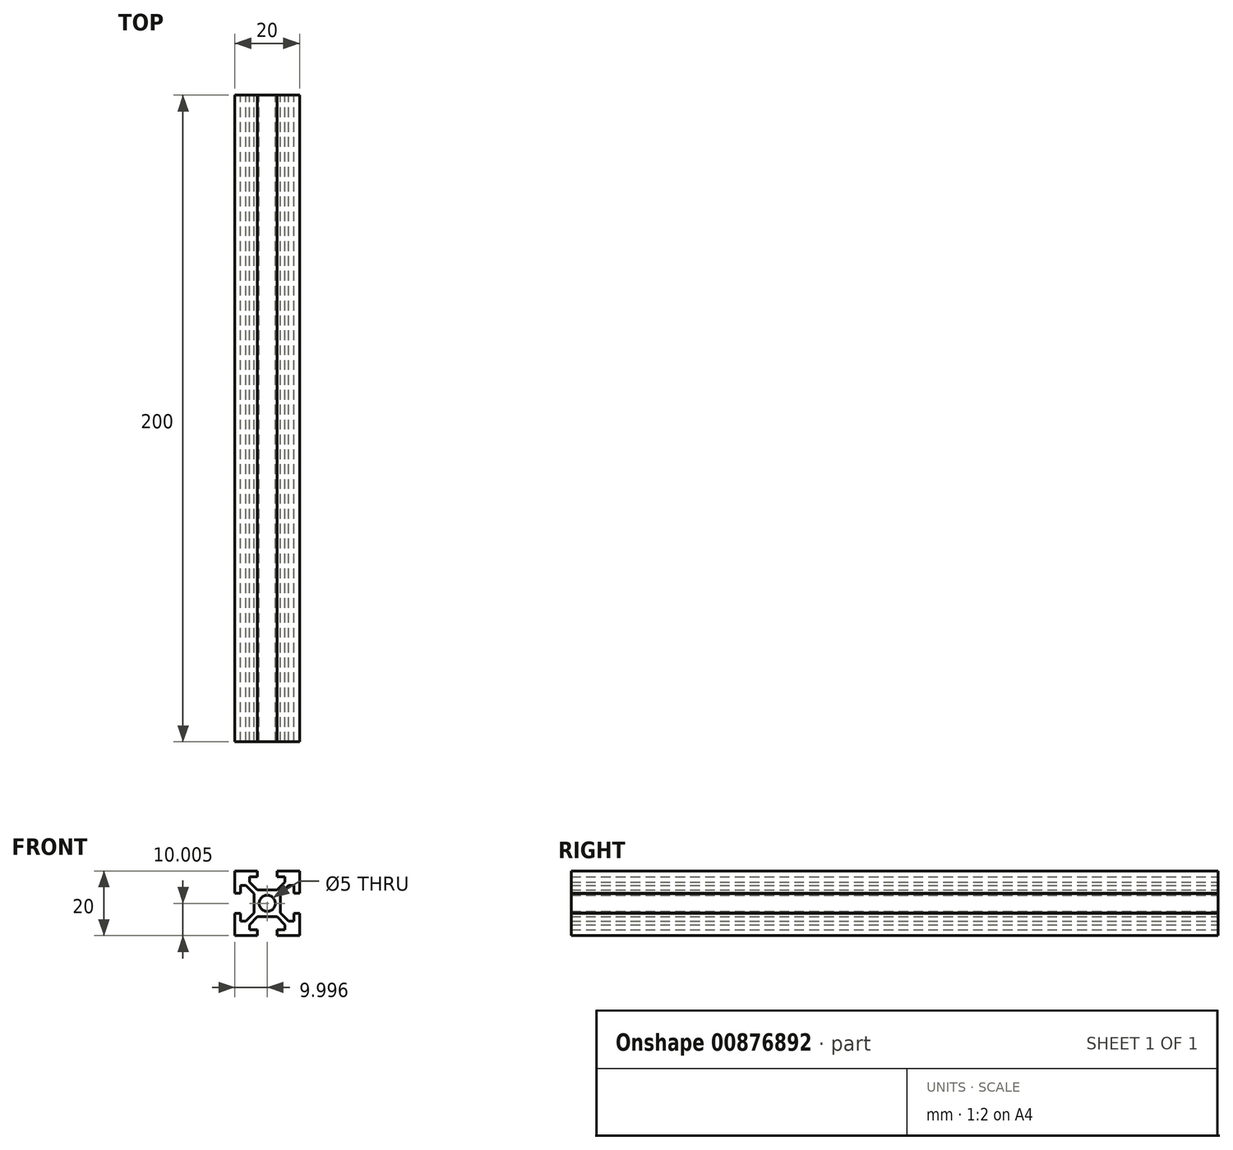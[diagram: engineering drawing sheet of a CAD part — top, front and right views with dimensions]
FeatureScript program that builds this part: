
annotation { "Feature Type Name" : "Feature", "Feature Type Description" : "" }
export const myFeature = defineFeature(function(context is Context, id is Id, definition is map)
    precondition{}
    {
        {
            var Q0;
            Q0=qCreatedBy(makeId("Front.planeOp"),FACE);
            var sketch = newSketch(context, id + "F0", { "sketchPlane" : qUnion([Q0])});
            skLineSegment(sketch, "E0.bottom", {"start": v(-42.2, 33.21) * mm, "end": v(-22.2, 33.21) * mm});
            skLineSegment(sketch, "E0.top", {"start": v(-42.2, 13.21) * mm, "end": v(-22.2, 13.21) * mm});
            skLineSegment(sketch, "E0.left", {"start": v(-42.2, 33.21) * mm, "end": v(-42.2, 13.21) * mm});
            skLineSegment(sketch, "E0.right", {"start": v(-22.2, 33.21) * mm, "end": v(-22.2, 13.21) * mm});
            skPoint(sketch, "E0.middle", {"position": v(-32.2, 23.21) * mm});
            skLineSegment(sketch, "E1", {"start": v(-24, 26.31) * mm, "end": v(-22.2, 26.31) * mm});
            skLineSegment(sketch, "E2.MirrorCS", {"start": v(-24, 20.11) * mm, "end": v(-22.2, 20.11) * mm});
            skLineSegment(sketch, "E3", {"start": v(-24, 26.31) * mm, "end": v(-24, 28.71) * mm});
            skLineSegment(sketch, "E4.MirrorCS", {"start": v(-24, 20.11) * mm, "end": v(-24, 17.71) * mm});
            skLineSegment(sketch, "E5", {"start": v(-24, 28.71) * mm, "end": v(-25.6, 28.71) * mm});
            skLineSegment(sketch, "E6.MirrorCS", {"start": v(-24, 17.71) * mm, "end": v(-25.6, 17.71) * mm});
            skCircle(sketch, "E7", {"center": v(-32.2, 23.21) * mm, "radius": 2.5 * mm});
            skLineSegment(sketch, "E8", {"start": v(-28.1, 26.21) * mm, "end": v(-28.1, 20.21) * mm});
            skLineSegment(sketch, "E9", {"start": v(-28.1, 26.21) * mm, "end": v(-25.6, 28.71) * mm});
            skLineSegment(sketch, "E10.MirrorCS", {"start": v(-28.1, 20.21) * mm, "end": v(-25.6, 17.71) * mm});
            skLineSegment(sketch, "E11.MirrorCS", {"start": v(-40.4, 26.31) * mm, "end": v(-42.2, 26.31) * mm});
            skLineSegment(sketch, "E12.MirrorCS", {"start": v(-40.4, 26.31) * mm, "end": v(-40.4, 28.71) * mm});
            skLineSegment(sketch, "E13.MirrorCS", {"start": v(-40.4, 28.71) * mm, "end": v(-38.8, 28.71) * mm});
            skLineSegment(sketch, "E14.MirrorCS", {"start": v(-36.3, 26.21) * mm, "end": v(-38.8, 28.71) * mm});
            skLineSegment(sketch, "E15.MirrorCS", {"start": v(-36.3, 26.21) * mm, "end": v(-36.3, 20.21) * mm});
            skLineSegment(sketch, "E16.MirrorCS", {"start": v(-36.3, 20.21) * mm, "end": v(-38.8, 17.71) * mm});
            skLineSegment(sketch, "E17.MirrorCS", {"start": v(-40.4, 17.71) * mm, "end": v(-38.8, 17.71) * mm});
            skLineSegment(sketch, "E18.MirrorCS", {"start": v(-40.4, 20.11) * mm, "end": v(-40.4, 17.71) * mm});
            skLineSegment(sketch, "E19.MirrorCS", {"start": v(-40.4, 20.11) * mm, "end": v(-42.2, 20.11) * mm});
            skLineSegment(sketch, "E20", {"start": v(-35.3, 33.21) * mm, "end": v(-35.3, 31.41) * mm});
            skLineSegment(sketch, "E21", {"start": v(-35.3, 31.41) * mm, "end": v(-37.7, 31.41) * mm});
            skLineSegment(sketch, "E22", {"start": v(-37.7, 31.41) * mm, "end": v(-37.7, 29.81) * mm});
            skLineSegment(sketch, "E23", {"start": v(-35.2, 27.31) * mm, "end": v(-32.2, 27.31) * mm});
            skLineSegment(sketch, "E24.MirrorCS", {"start": v(-29.1, 33.21) * mm, "end": v(-29.1, 31.41) * mm});
            skLineSegment(sketch, "E25.MirrorCS", {"start": v(-29.1, 31.41) * mm, "end": v(-26.7, 31.41) * mm});
            skLineSegment(sketch, "E26.MirrorCS", {"start": v(-26.7, 31.41) * mm, "end": v(-26.7, 29.81) * mm});
            skLineSegment(sketch, "E27.MirrorCS", {"start": v(-29.2, 27.31) * mm, "end": v(-32.2, 27.31) * mm});
            skLineSegment(sketch, "E28", {"start": v(-26.7, 29.81) * mm, "end": v(-29.2, 27.31) * mm});
            skLineSegment(sketch, "E29", {"start": v(-37.7, 29.81) * mm, "end": v(-35.2, 27.31) * mm});
            skLineSegment(sketch, "E30.MirrorCS", {"start": v(-35.3, 13.21) * mm, "end": v(-35.3, 15.01) * mm});
            skLineSegment(sketch, "E31.MirrorCS", {"start": v(-35.3, 15.01) * mm, "end": v(-37.7, 15.01) * mm});
            skLineSegment(sketch, "E32.MirrorCS", {"start": v(-37.7, 15.01) * mm, "end": v(-37.7, 16.61) * mm});
            skLineSegment(sketch, "E33.MirrorCS", {"start": v(-37.7, 16.61) * mm, "end": v(-35.2, 19.11) * mm});
            skLineSegment(sketch, "E34.MirrorCS", {"start": v(-29.1, 13.21) * mm, "end": v(-29.1, 15.01) * mm});
            skLineSegment(sketch, "E35.MirrorCS", {"start": v(-29.1, 15.01) * mm, "end": v(-26.7, 15.01) * mm});
            skLineSegment(sketch, "E36.MirrorCS", {"start": v(-26.7, 15.01) * mm, "end": v(-26.7, 16.61) * mm});
            skLineSegment(sketch, "E37.MirrorCS", {"start": v(-26.7, 16.61) * mm, "end": v(-29.2, 19.11) * mm});
            skLineSegment(sketch, "E38.MirrorCS", {"start": v(-29.2, 19.11) * mm, "end": v(-32.2, 19.11) * mm});
            skLineSegment(sketch, "E39.MirrorCS", {"start": v(-35.2, 19.11) * mm, "end": v(-32.2, 19.11) * mm});
            skSolve(sketch);
        }
        {
            var Q0;
            {var subQ5=sQuery(id+"F0.wireOp",EDGE,"E1");Q0=makeQuery(id+"F0.imprint","IMPRINT",FACE,{"disambiguationData":[TD([[makeQuery(id+"F0.imprint","IMPRINT",EDGE,{"derivedFrom":subQ5}),1.0]])]});}
            extrude(context, id + "F1", {"entities" : qUnion([Q0]), "depth" : 200 * mm, "offsetDistance" : 25 * mm});
        }
    });
